# Revit family: LeL Reiko 2.0
name_source: partatom
category: Lighting Fixtures
units: mm (PartAtom-declared; Revit-internal decimal feet)

## family parameters
Always vertical = No
Cut with Voids When Loaded = No
Light Source = No
OmniClass Number = 23.80.70.00
OmniClass Title = Lighting
Part Type = Normal
Room Calculation Point = No
Round Connector Dimension = Use Diameter
Shared = No
Work Plane-Based = Yes

## types (23) — shared parameters
CCT = 3000 K
CRI = CRI80
Default Elevation = 1219 mm
Description = Outdoor Projectors
IK = IK06
IP = IP66
Lamp = LED
Manufacturer = L&L Luce&Light srl
Model = RK20
Rated Power supply = 24 V
URL = https://www.lucelight.it
Weight = 0.50 kg

## per-type parameters (varying)
| type | Apparent Load | Lumen Output | Photometry | Wattage |
| J 49° 5W | 5 VA | 280 lm | RK20 Light source : J 49° 5W | 5 W |
| K 73° 5W | 5 VA | 243 lm | RK20 Light source : K 73° 5W | 5 W |
| L 44° 5W | 5 VA | 280 lm | RK20 Light source : L 44° 5W | 5 W |
| M 34° 5W | 5 VA | 280 lm | RK20 Light source : M 34° 5W | 5 W |
| P (22°) 5W | 5 VA | 217 lm | RK20 Light source : P (22°) 5W | 5 W |
| Q (56°) 5W | 5 VA | 172 lm | RK20 Light source : Q (56°) 5W | 5 W |
| S 18° 5W | 5 VA | 302 lm | RK20 Light source : S 18° 5W | 5 W |
| T 15° 5W | 5 VA | 288 lm | RK20 Light source : T 15° 5W | 5 W |
| W 16°x50° 5W | 5 VA | 268 lm | RK20 Light source : W 16°x50° 5W | 5 W |
| X 50°x16° 5W | 5 VA | 272 lm | RK20 Light source : X 50°x16° 5W | 5 W |
| J 49° 7W | 7 VA | 278 lm | RK20 Light source : J 49° 7W | 7 W |
| V 8° 5W | 5 VA | 286 lm | RK20 Light source : V 8° 5W | 5 W |
| K 73° 7W | 5 VA | 328 lm | RK20 Light source : K 73° 7W | 5 W |
| L 44° 7W | 7 VA | 377 lm | RK20 Light source : L 44° 7W | 7 W |
| M 34° 7W | 7 VA | 363 lm | RK20 Light source : M 34° 7W | 7 W |
| P (22°) 7W | 7 VA | 293 lm | RK20 Light source : P (22°) 7W | 7 W |
| Q (56°) 7W | 7 VA | 232 lm | RK20 Light source : Q (56°) 7W | 7 W |
| S 18° 7W | 7 VA | 407 lm | RK20 Light source : S 18° 7W | 7 W |
| T 15° 7W | 7 VA | 388 lm | RK20 Light source : T 15° 7W | 7 W |
| V 8° 7W | 7 VA | 386 lm | RK20 Light source : V 8° 7W | 7 W |
| W 16°x50° 7W | 7 VA | 361 lm | RK20 Light source : W 16°x50° 7W | 7 W |
| X 50°x16° 7W | 7 VA | 367 lm | RK20 Light source : X 50°x16° 7W | 7 W |
| U 5° 3.5W | 4 VA | 136 lm | RK20 Light source : U 5° 3.5W | 4 W |

## geometry (parser evidence)
native form markers: Sweep x2
no freeform markers — native parametric forms only
